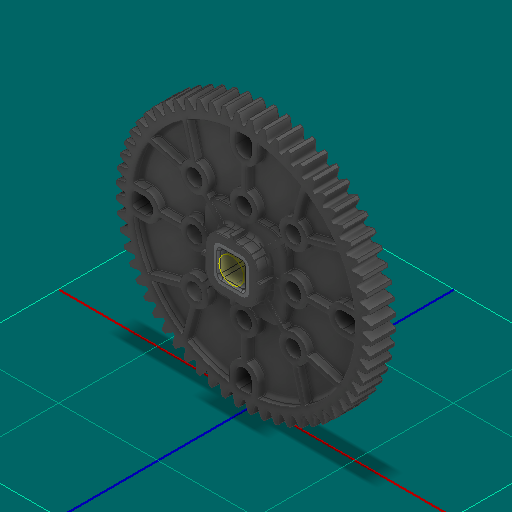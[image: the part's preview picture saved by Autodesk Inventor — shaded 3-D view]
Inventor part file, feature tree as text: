
AUTODESK INVENTOR PART (.ipt)
format: ipt  version: 2025 (Build 290162000, 162)  size: 4,805,120 bytes
history: native  units: in
note: dims shown in document units (in); Inventor stores cm internally (conversion verified against a paired STEP export)
features: other x6, sketch x3
ambient origin geometry x8: Origin, YZ Plane, XZ Plane, XY Plane, X Axis, Y Axis, Z Axis, Center Point
bodies: Solid1 (feature_tree), Solid2 (feature_tree)
feature tree (9):
  other  "Half Cut HS 60T Gear.ipt"
  other  "Solid1::Half Cut HS 60T Gear.ipt"
  other  "Solid2::Half Cut HS 60T Gear.ipt"
  other  "TaggingFeature1"
  sketch  "Sketch1"  dims[d0=0.3937in]
  sketch  "Sketch2"
  sketch  "Sketch3"
  other  "Srf1"
  other  "Srf1::Derived"
